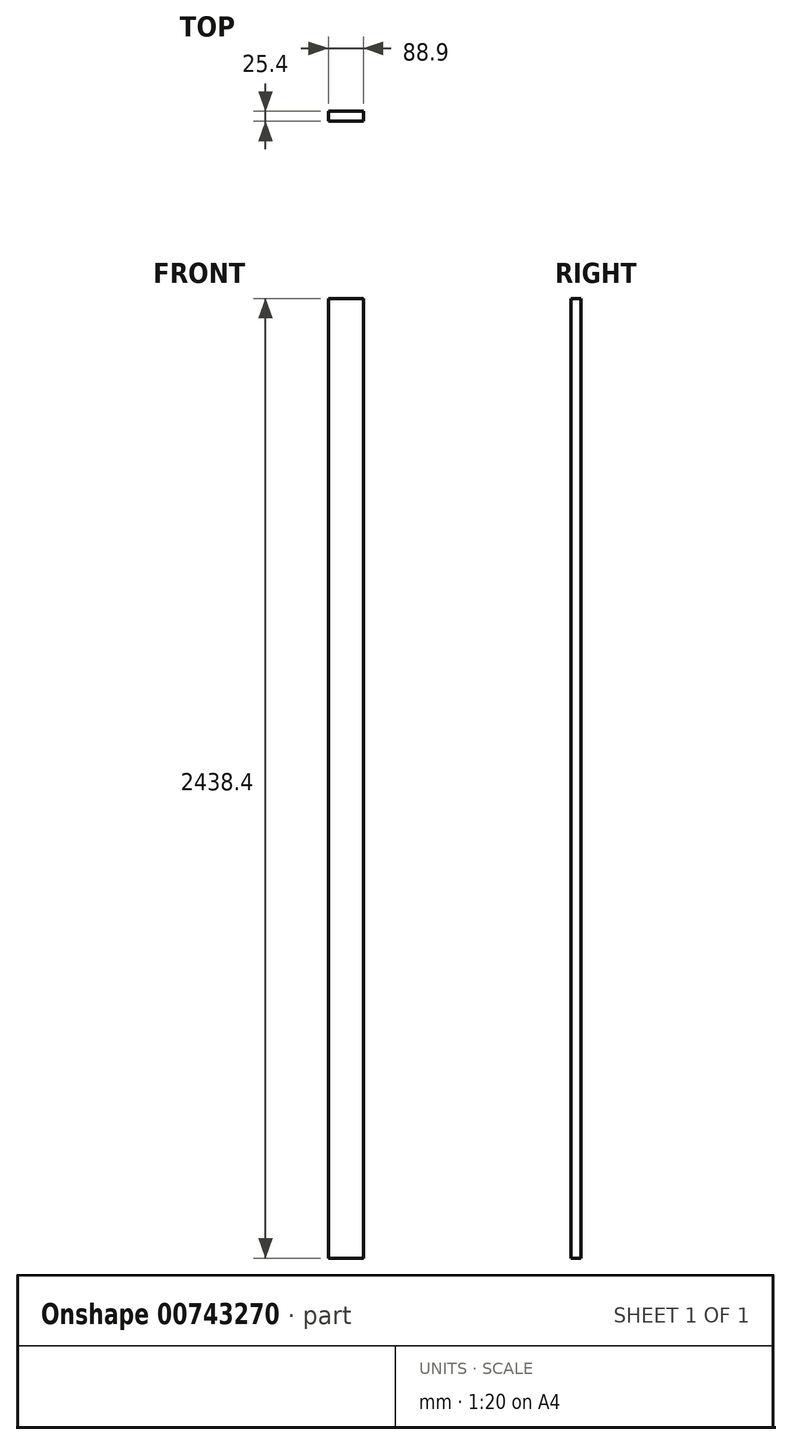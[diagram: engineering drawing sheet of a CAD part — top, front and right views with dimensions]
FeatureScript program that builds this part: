
annotation { "Feature Type Name" : "Feature", "Feature Type Description" : "" }
export const myFeature = defineFeature(function(context is Context, id is Id, definition is map)
    precondition{}
    {
        {
            var Q0;
            Q0=qCreatedBy(makeId("Front.planeOp"),FACE);
            var sketch = newSketch(context, id + "F0", { "sketchPlane" : qUnion([Q0])});
            skLineSegment(sketch, "E0.bottom", {"start": v(0, 0) * mm, "end": v(88.9, 0) * mm});
            skLineSegment(sketch, "E0.top", {"start": v(0, 2438.4) * mm, "end": v(88.9, 2438.4) * mm});
            skLineSegment(sketch, "E0.left", {"start": v(0, 0) * mm, "end": v(0, 2438.4) * mm});
            skLineSegment(sketch, "E0.right", {"start": v(88.9, 0) * mm, "end": v(88.9, 2438.4) * mm});
            skSolve(sketch);
        }
        {
            var Q0;
            Q0 = qSketchRegion(id + "F0", true);
            extrude(context, id + "F1", {"entities" : qUnion([Q0]), "depth" : 25.4 * mm, "offsetDistance" : 25.4 * mm});
        }
    });
